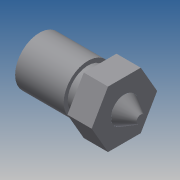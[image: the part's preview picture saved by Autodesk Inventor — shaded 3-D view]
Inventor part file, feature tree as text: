
AUTODESK INVENTOR PART (.ipt)
format: ipt  version: 2013 (Build 170138000, 138)  size: 104,448 bytes
history: native  units: mm
features: sketch x2, revolve x1, extrude x1
ambient origin geometry x8: Origin, YZ Plane, XZ Plane, XY Plane, X Axis, Y Axis, Z Axis, Center Point
bodies: Solid1 (feature_tree)
feature tree (4):
  revolve  "Revolution1"  [1 undecoded]
  extrude  "Extrusion1"  Depth=10.0mm
  sketch  "Sketch1"  dims[d0=0.5mm d3=3.0mm]
  sketch  "Sketch2"  dims[d5=2.5mm d6=10.0mm d7=10.5mm d8=2.0mm d9=30.0deg d10=7.5mm d11=6.0mm d12=90.0deg d13=7.0mm d14=10.0mm d15=0.0mm]
note: 1 required parameter value undecoded (feature->parameter linkage not recoverable at this tier; creation-order binding heuristic only, values carry confidence <= 0.55)
